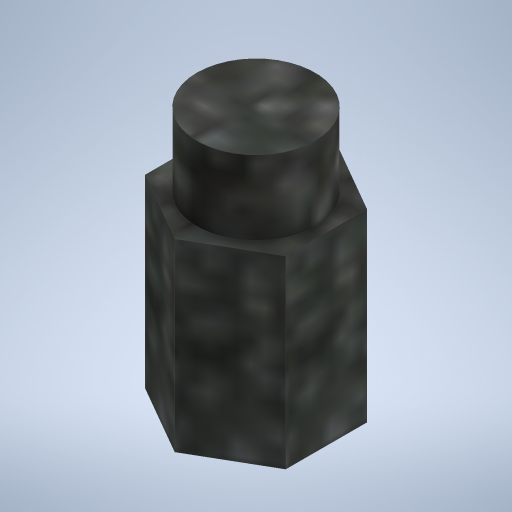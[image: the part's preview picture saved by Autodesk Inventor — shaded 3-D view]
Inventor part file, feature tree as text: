
AUTODESK INVENTOR PART (.ipt)
format: ipt  version: 2023 (Build 270158030, 158C)  size: 302,592 bytes
history: native  units: in
note: dims shown in document units (in); Inventor stores cm internally (conversion verified against a paired STEP export)
features: extrude x2, sketch x2
ambient origin geometry x8: Origin, YZ Plane, XZ Plane, XY Plane, X Axis, Y Axis, Z Axis, Center Point
bodies: Solid1 (feature_tree)
feature tree (4):
  extrude  "Extrusion1"  Depth=0.4921in TaperAngle=0.0deg
  extrude  "Extrusion2"  Depth=0.1969in TaperAngle=0.0deg
  sketch  "Sketch1"  dims[d0=0.375in d1=0.4921in d2=0.0in]
  sketch  "Sketch2"  dims[d3=0.315in d4=0.1969in d5=0.0in d11=0.835in d12=0.0in]
